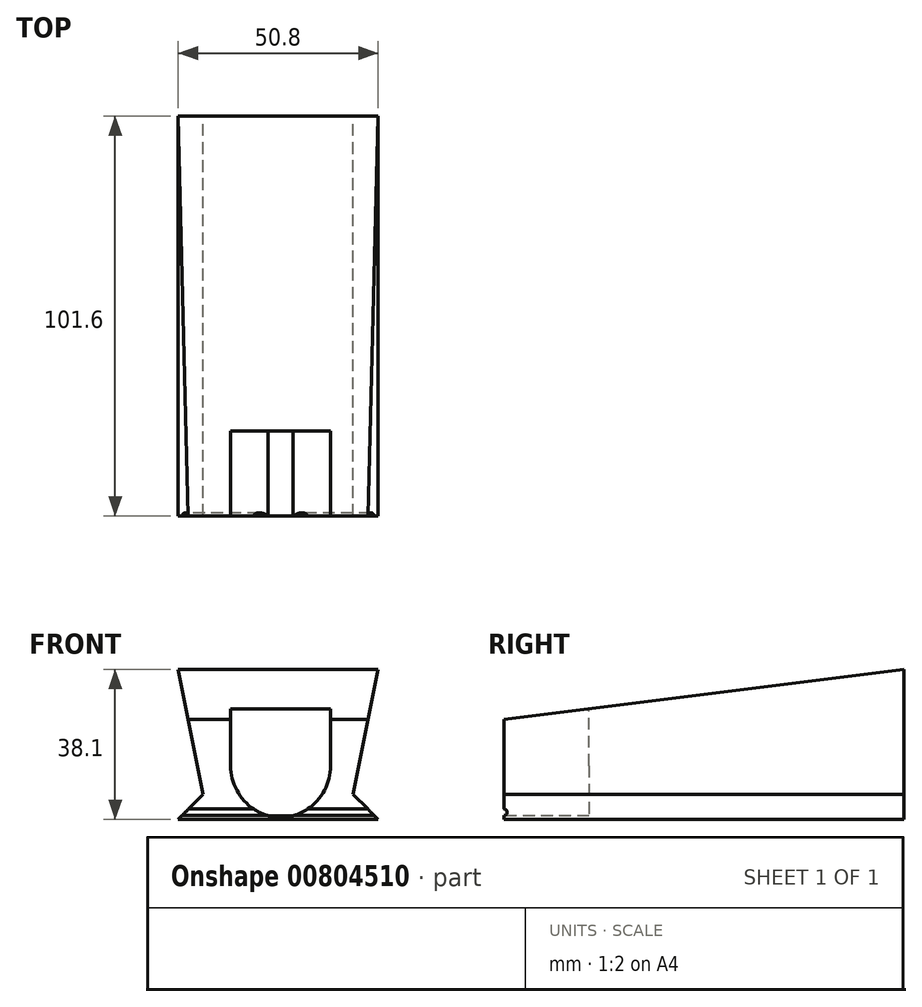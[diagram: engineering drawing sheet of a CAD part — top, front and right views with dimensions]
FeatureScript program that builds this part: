
annotation { "Feature Type Name" : "Feature", "Feature Type Description" : "" }
export const myFeature = defineFeature(function(context is Context, id is Id, definition is map)
    precondition{}
    {
        {
            var Q0;
            Q0=qCreatedBy(makeId("Front.planeOp"),FACE);
            var sketch = newSketch(context, id + "F0", { "sketchPlane" : qUnion([Q0])});
            skLineSegment(sketch, "E0", {"start": v(0, 0) * mm, "end": v(6.35, 0) * mm, "construction": true});
            skLineSegment(sketch, "E1", {"start": v(6.35, 0) * mm, "end": v(44.45, 0) * mm, "construction": true});
            skLineSegment(sketch, "E2", {"start": v(44.45, 0) * mm, "end": v(50.8, 0) * mm, "construction": true});
            skLineSegment(sketch, "E3", {"start": v(0, 0) * mm, "end": v(0, 31.75) * mm, "construction": true});
            skLineSegment(sketch, "E4", {"start": v(0, 31.75) * mm, "end": v(6.35, 0) * mm});
            skLineSegment(sketch, "E5", {"start": v(6.35, 0) * mm, "end": v(44.45, 0) * mm});
            skLineSegment(sketch, "E6", {"start": v(50.8, 0) * mm, "end": v(50.8, 31.75) * mm, "construction": true});
            skLineSegment(sketch, "E7", {"start": v(50.8, 31.75) * mm, "end": v(44.45, 0) * mm});
            skLineSegment(sketch, "E8", {"start": v(50.8, 31.75) * mm, "end": v(0, 31.75) * mm});
            skLineSegment(sketch, "E9", {"start": v(0, 0) * mm, "end": v(0, -6.35) * mm, "construction": true});
            skLineSegment(sketch, "E10", {"start": v(6.35, 0) * mm, "end": v(0, -6.35) * mm});
            skLineSegment(sketch, "E11", {"start": v(0, -6.35) * mm, "end": v(50.8, -6.35) * mm});
            skLineSegment(sketch, "E12", {"start": v(50.8, -6.35) * mm, "end": v(44.45, 0) * mm});
            skSolve(sketch);
        }
        {
            var Q0;
            Q0 = qSketchRegion(id + "F0", true);
            extrude(context, id + "F1", {"entities" : qUnion([Q0]), "depth" : 101.6 * mm, "offsetDistance" : 25.4 * mm});
        }
        {
            var Q0;
            Q0=qCreatedBy(makeId("Right.planeOp"),FACE);
            var sketch = newSketch(context, id + "F2", { "sketchPlane" : qUnion([Q0])});
            skLineSegment(sketch, "E13", {"start": v(0, 0) * mm, "end": v(0, 31.75) * mm});
            skLineSegment(sketch, "E14", {"start": v(0, 31.75) * mm, "end": v(-101.6, 31.75) * mm, "construction": true});
            skLineSegment(sketch, "E15", {"start": v(-101.6, 31.75) * mm, "end": v(-101.6, 19.05) * mm, "construction": true});
            skLineSegment(sketch, "E16", {"start": v(-101.6, 19.05) * mm, "end": v(0, 31.75) * mm});
            skLineSegment(sketch, "E17", {"start": v(-101.6, 31.75) * mm, "end": v(0, 31.75) * mm});
            skLineSegment(sketch, "E18", {"start": v(-101.6, 31.75) * mm, "end": v(-101.6, 19.05) * mm});
            skSolve(sketch);
        }
        {
            var Q0;
            Q0 = qSketchRegion(id + "F2", true);
            extrude(context, id + "F3", {"entities" : qUnion([Q0]), "operationType" : NewBodyOperationType.REMOVE, "depth" : 50.8 * mm, "offsetDistance" : 25.4 * mm});
        }
        {
            var Q0;
            Q0=makeQuery(id+"F1.opExtrude","CAP_FACE",FACE,{"disambiguationData":[OSD([sQuery(id+"F0.wireOp",EDGE,"E4"),sQuery(id+"F0.wireOp",EDGE,"E7"),sQuery(id+"F0.wireOp",EDGE,"E8"),sQuery(id+"F0.wireOp",EDGE,"E10"),sQuery(id+"F0.wireOp",EDGE,"E11"),sQuery(id+"F0.wireOp",EDGE,"E12")])],"isStart":false});
            var sketch = newSketch(context, id + "F4", { "sketchPlane" : qUnion([Q0])});
            skLineSegment(sketch, "E19", {"start": v(38.74, -2.87) * mm, "end": v(13.34, -2.87) * mm, "construction": true});
            skLineSegment(sketch, "E20", {"start": v(13.34, -2.87) * mm, "end": v(13.34, 7.29) * mm, "construction": true});
            skLineSegment(sketch, "E21", {"start": v(38.74, -2.87) * mm, "end": v(38.74, 7.29) * mm, "construction": true});
            skLineSegment(sketch, "E22", {"start": v(13.34, 7.29) * mm, "end": v(13.34, 26.34) * mm});
            skLineSegment(sketch, "E23", {"start": v(13.34, 26.34) * mm, "end": v(38.74, 26.34) * mm});
            skLineSegment(sketch, "E24", {"start": v(38.74, 26.34) * mm, "end": v(38.74, 7.29) * mm});
            skLineSegment(sketch, "E25", {"start": v(26.04, 7.29) * mm, "end": v(26.04, -5.41) * mm, "construction": true});
            skLineSegment(sketch, "E26", {"start": v(26.04, -5.41) * mm, "end": v(29.21, -5.41) * mm, "construction": true});
            skLineSegment(sketch, "E27", {"start": v(29.21, -5.41) * mm, "end": v(22.86, -5.41) * mm, "construction": true});
            skLineSegment(sketch, "E28", {"start": v(22.86, -5.41) * mm, "end": v(29.21, -5.41) * mm});
            skArc(sketch, "E29", {"start": v(13.34, 7.29) * mm, "mid": v(15.98, -0.65) * mm, "end": v(22.86, -5.41) * mm});
            skArc(sketch, "E30", {"start": v(29.21, -5.41) * mm, "mid": v(36.09, -0.65) * mm, "end": v(38.74, 7.29) * mm});
            skSolve(sketch);
        }
        {
            var Q0;
            Q0=makeQuery(id+"F4.imprint","IMPRINT",FACE,{"disambiguationData":[TD([[makeQuery(id+"F4.imprint","IMPRINT",EDGE,{"derivedFrom":sQuery(id+"F4.wireOp",EDGE,"d72acfc9-cf68-4604-b08e-1613f7bc9844")}),1.0]])]});
            var Q1;
            {var subQ0=sQuery(id+"F4.wireOp",EDGE,"E23");Q1=makeQuery(id+"F4.imprint","IMPRINT",FACE,{"disambiguationData":[TD([[makeQuery(id+"F4.imprint","IMPRINT",EDGE,{"derivedFrom":subQ0}),-1.0]])]});}
            var Q2;
            Q2=makeQuery(id+"F4.imprint","IMPRINT",FACE,{"disambiguationData":[TD([[makeQuery(id+"F4.imprint","IMPRINT",EDGE,{"derivedFrom":sQuery(id+"F4.wireOp",EDGE,"E28")}),1.0]])]});
            extrude(context, id + "F5", {"entities" : qUnion([Q0, Q1, Q2]), "operationType" : NewBodyOperationType.REMOVE, "oppositeDirection" : true, "depth" : 21.59 * mm, "offsetDistance" : 25.4 * mm});
        }
        {
            var Q0;
            Q0=qCreatedBy(makeId("Right.planeOp"),FACE);
            cPlane(context, id + "F6", {"entities" : qUnion([Q0]), "cplaneType" : CPlaneType.OFFSET, "offset" : 26.03 * mm, "width" : 152.4 * mm, "height" : 152.4 * mm});
        }
        {
            var Q0;
            Q0=qCreatedBy(id+"F6.planeOp",FACE);
            var sketch = newSketch(context, id + "F7", { "sketchPlane" : qUnion([Q0])});
            skLineSegment(sketch, "E31", {"start": v(0, 0) * mm, "end": v(-101.6, 0) * mm, "construction": true});
            skLineSegment(sketch, "E32", {"start": v(-101.6, 0) * mm, "end": v(-101.6, -6.35) * mm, "construction": true});
            skLineSegment(sketch, "E33", {"start": v(-101.6, -6.35) * mm, "end": v(-101.6, -5.41) * mm, "construction": true});
            skLineSegment(sketch, "E34", {"start": v(-101.6, -5.41) * mm, "end": v(-101.6, -4.52) * mm, "construction": true});
            skCircle(sketch, "E35", {"center": v(-101.6, -4.52) * mm, "radius": 0.8 * mm, "construction": true});
            skCircle(sketch, "E36", {"center": v(-101.6, -4.52) * mm, "radius": 0.8 * mm});
            skSolve(sketch);
        }
        {
            var Q0;
            Q0 = qSketchRegion(id + "F7", true);
            extrude(context, id + "F8", {"entities" : qUnion([Q0]), "operationType" : NewBodyOperationType.REMOVE, "endBound" : BoundingType.SYMMETRIC, "depth" : 50.8 * mm, "offsetDistance" : 25.4 * mm});
        }
    });
